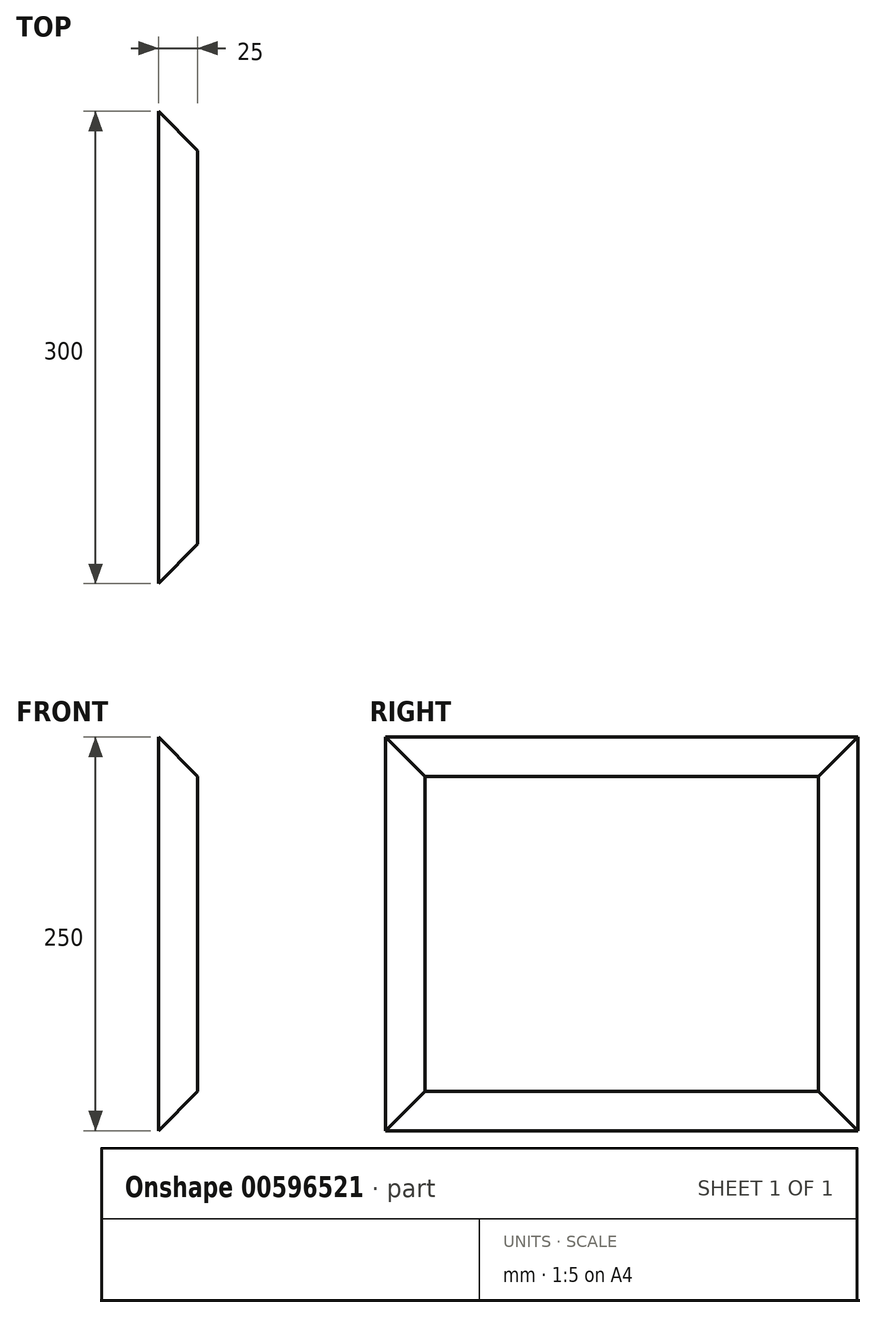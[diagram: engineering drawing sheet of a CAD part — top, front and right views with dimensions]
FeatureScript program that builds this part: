
annotation { "Feature Type Name" : "Feature", "Feature Type Description" : "" }
export const myFeature = defineFeature(function(context is Context, id is Id, definition is map)
    precondition{}
    {
        {
            var Q0;
            Q0=qCreatedBy(makeId("Right.planeOp"),FACE);
            var sketch = newSketch(context, id + "F0", { "sketchPlane" : qUnion([Q0])});
            skLineSegment(sketch, "E0.bottom", {"start": v(150, -125) * mm, "end": v(-150, -125) * mm});
            skLineSegment(sketch, "E0.top", {"start": v(150, 125) * mm, "end": v(-150, 125) * mm});
            skLineSegment(sketch, "E0.left", {"start": v(150, -125) * mm, "end": v(150, 125) * mm});
            skLineSegment(sketch, "E0.right", {"start": v(-150, -125) * mm, "end": v(-150, 125) * mm});
            skPoint(sketch, "E0.middle", {"position": v(0, 0) * mm});
            skSolve(sketch);
        }
        {
            var Q0;
            Q0=makeQuery(id+"F0.imprint","IMPRINT",FACE,{"disambiguationData":[TD([[makeQuery(id+"F0.imprint","IMPRINT",EDGE,{"derivedFrom":sQuery(id+"F0.wireOp",EDGE,"E0.bottom")}),-1.0]])]});
            extrude(context, id + "F1", {"entities" : qUnion([Q0]), "oppositeDirection" : true, "depth" : 25 * mm, "offsetDistance" : 25 * mm});
        }
        {
            var Q0;
            Q0=makeQuery(id+"F1.opExtrude","CAP_EDGE",EDGE,{"disambiguationData":[OSD([sQuery(id+"F0.wireOp",EDGE,"E0.top")])],"isStart":true});
            var Q1;
            Q1=makeQuery(id+"F1.opExtrude","CAP_EDGE",EDGE,{"disambiguationData":[OSD([sQuery(id+"F0.wireOp",EDGE,"E0.right")])],"isStart":true});
            var Q2;
            Q2=makeQuery(id+"F1.opExtrude","CAP_EDGE",EDGE,{"disambiguationData":[OSD([sQuery(id+"F0.wireOp",EDGE,"E0.bottom")])],"isStart":true});
            var Q3;
            Q3=makeQuery(id+"F1.opExtrude","CAP_EDGE",EDGE,{"disambiguationData":[OSD([sQuery(id+"F0.wireOp",EDGE,"E0.left")])],"isStart":true});
            chamfer(context, id + "F2", {"entities" : qUnion([Q0, Q1, Q2, Q3]), "width" : 25 * mm, "tangentPropagation" : true});
        }
    });
